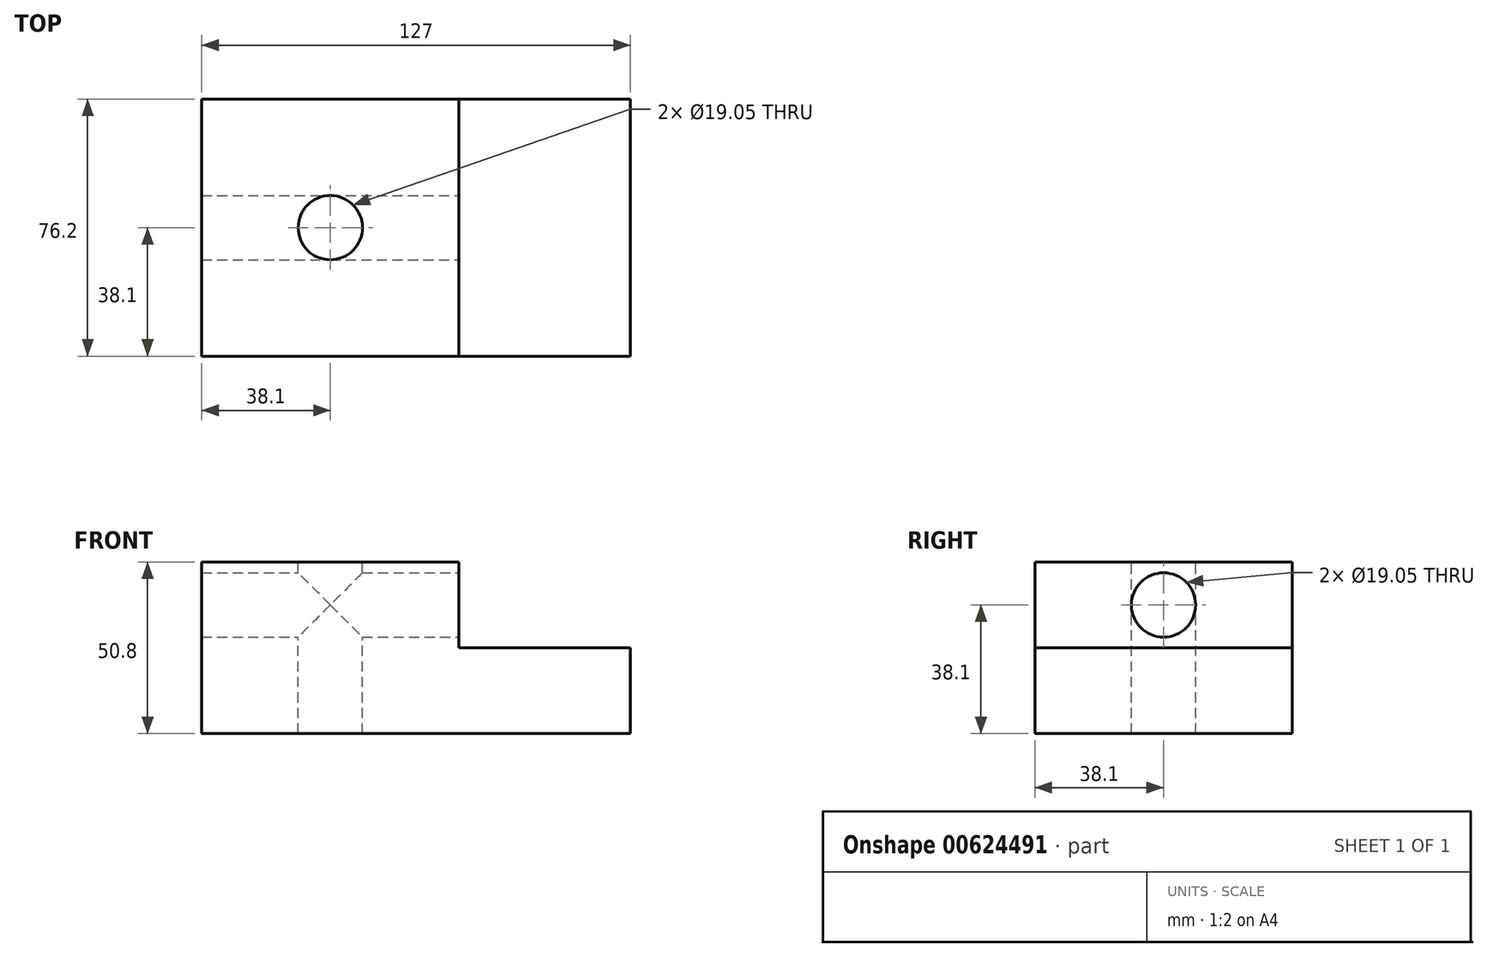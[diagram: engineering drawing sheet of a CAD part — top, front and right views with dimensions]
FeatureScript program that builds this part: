
annotation { "Feature Type Name" : "Feature", "Feature Type Description" : "" }
export const myFeature = defineFeature(function(context is Context, id is Id, definition is map)
    precondition{}
    {
        {
            var Q0;
            Q0=qCreatedBy(makeId("Front.planeOp"),FACE);
            var sketch = newSketch(context, id + "F0", { "sketchPlane" : qUnion([Q0])});
            skLineSegment(sketch, "E0.bottom", {"start": v(0, 0) * mm, "end": v(127, 0) * mm});
            skLineSegment(sketch, "E0.top", {"start": v(0, 50.8) * mm, "end": v(127, 50.8) * mm});
            skLineSegment(sketch, "E0.left", {"start": v(0, 0) * mm, "end": v(0, 50.8) * mm});
            skLineSegment(sketch, "E0.right", {"start": v(127, 0) * mm, "end": v(127, 50.8) * mm});
            skLineSegment(sketch, "E1", {"start": v(127, 25.4) * mm, "end": v(76.2, 25.4) * mm});
            skLineSegment(sketch, "E2", {"start": v(76.2, 25.4) * mm, "end": v(76.2, 50.8) * mm});
            skSolve(sketch);
        }
        {
            var Q0;
            {var subQ1=sQuery(id+"F0.wireOp",EDGE,"E0.bottom");Q0=makeQuery(id+"F0.imprint","IMPRINT",FACE,{"disambiguationData":[TD([[makeQuery(id+"F0.imprint","IMPRINT",EDGE,{"derivedFrom":subQ1}),1.0]])]});}
            extrude(context, id + "F1", {"entities" : qUnion([Q0]), "depth" : 76.2 * mm, "offsetDistance" : 25.4 * mm});
        }
        {
            var Q0;
            Q0=makeQuery(id+"F1.opExtrude","SWEPT_FACE",FACE,{"disambiguationData":[OSD([sQuery(id+"F0.wireOp",EDGE,"E0.top")])]});
            var sketch = newSketch(context, id + "F2", { "sketchPlane" : qUnion([Q0])});
            skPoint(sketch, "E3", {"position": v(38.1, 0) * mm});
            skPoint(sketch, "E4", {"position": v(0, -38.1) * mm});
            skPoint(sketch, "E5", {"position": v(38.1, -38.1) * mm});
            skSolve(sketch);
        }
        {
            var Q0;
            Q0=sQuery(id+"F2.wireOp",VERTEX,"E5");
            var Q1;
            Q1=makeQuery(id+"F1.opExtrude","SWEPT_BODY",BODY,{"disambiguationData":[OSD([sQuery(id+"F0.wireOp",EDGE,"E0.bottom"),sQuery(id+"F0.wireOp",EDGE,"E0.top"),sQuery(id+"F0.wireOp",EDGE,"E0.left"),sQuery(id+"F0.wireOp",EDGE,"E0.right"),sQuery(id+"F0.wireOp",EDGE,"E1"),sQuery(id+"F0.wireOp",EDGE,"E2")])]});
            hole(context, id + "F3", {"style" : HoleStyle.SIMPLE, "endStyle" : HoleEndStyle.THROUGH, "holeDiameter" : 19.05 * mm, "majorDiameter" : 6.35 * mm, "isTappedThrough" : true, "tappedDepth" : 12.7 * mm, "tapClearance" : 3, "locations" : qUnion([Q0]), "scope" : qUnion([Q1])});
        }
        {
            var Q0;
            Q0=makeQuery(id+"F1.opExtrude","SWEPT_FACE",FACE,{"disambiguationData":[OSD([sQuery(id+"F0.wireOp",EDGE,"E2")])]});
            var sketch = newSketch(context, id + "F4", { "sketchPlane" : qUnion([Q0])});
            skPoint(sketch, "E6", {"position": v(0, 38.1) * mm});
            skPoint(sketch, "E7", {"position": v(-38.1, 25.4) * mm});
            skPoint(sketch, "E8", {"position": v(-38.1, 38.1) * mm});
            skSolve(sketch);
        }
        {
            var Q0;
            Q0=sQuery(id+"F4.wireOp",VERTEX,"E8");
            var Q1;
            Q1=makeQuery(id+"F1.opExtrude","SWEPT_BODY",BODY,{"disambiguationData":[OSD([sQuery(id+"F0.wireOp",EDGE,"E0.bottom"),sQuery(id+"F0.wireOp",EDGE,"E0.top"),sQuery(id+"F0.wireOp",EDGE,"E0.left"),sQuery(id+"F0.wireOp",EDGE,"E0.right"),sQuery(id+"F0.wireOp",EDGE,"E1"),sQuery(id+"F0.wireOp",EDGE,"E2")])]});
            hole(context, id + "F5", {"style" : HoleStyle.SIMPLE, "endStyle" : HoleEndStyle.THROUGH, "holeDiameter" : 19.05 * mm, "majorDiameter" : 6.35 * mm, "isTappedThrough" : true, "tappedDepth" : 12.7 * mm, "tapClearance" : 3, "locations" : qUnion([Q0]), "scope" : qUnion([Q1])});
        }
    });
